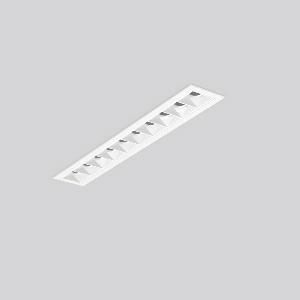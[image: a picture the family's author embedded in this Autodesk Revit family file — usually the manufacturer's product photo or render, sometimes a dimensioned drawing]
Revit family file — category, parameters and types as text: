
# Revit family: beamline_slim_641326_0025_2_76_4d5e
name_source: partatom
category: Lighting Fixtures
units: mm (PartAtom-declared; Revit-internal decimal feet)

## family parameters
Cut with Voids When Loaded = No
Host = Face
Light Source = No
Part Type = Normal
Room Calculation Point = No
Round Connector Dimension = Use Diameter
Shared = No

## types (1)
- BEAMLINE SLIM (1 x LED Modul 940, 2100 lm, 4000)
    Apparent Load = 25 VA
    CIE Flux Codes = 100 100 100 100 100
    Color Rendering = 92
    Color Temperature = 4000
    Default Elevation = 1800 mm
    Description = Series: BEAMLINE SLIM
Minimalistic recessed ceiling luminaire for aesthetically sophisticated lighting. Housing: metal, powder-coated. Perfect heat management with an aluminium heat sink. LED light unit with MRS technology: Mini-Reflector-System made of metallised thermoplastic with prismatic white glare-suppressing frame for pleasant glare-free light (RUG < 10). Narrow beam light distribution. Ceiling installation with spring system. Including separate LED converter with connecting cable 450 mm. 
Colour: traffic white, matt (RAL 9016)
Length: 295 mm
Width: 45 mm
Height: 1.5 mm
Cut-out length: 290 mm
Cut-out width: 40 mm
Recess height: 110 mm
Luminaire: recess height: 60 mm
Lamp: LED
Socket: without socket
Colour temperature: 4000K
Colour rendering index (CRI): 90
System power: 25 W
Rated luminous flux: 2100 lm
Luminous efficiency: 84 lm/W
Control gear: Converter, dimmable, DALI
Protection class: II
Type of protection: IP 20
    Height = 0 mm  [stored 0 ft]
    Lamp = 1 x LED Modul 940
    Lamp Light Flux = 2100 lm
    Lamp count = 1
    Length = 295 mm
    Lifetime = 50000 h
    Luminous efficacy = 84 lm/W
    Manufacturer = RZB
    ModVariant = No
    Model = 641326.0025.2.76
    Mounting Place = Ceiling
    Mounting Type = Recessed
    Number of Poles = 1
    OnlyDefault = Yes
    Power Factor = 1
    Product Name = BEAMLINE SLIM
    Product group = Recessed LED linear luminaires
    ProductGroupID = 407
    Protection Class = Protection class II
    Protection Degree = IP 20
    RLX_Detail_Level = 1
    RLX_Emergency_Light_Flux = 0 lm
    RLX_Emergency_Type = 0
    RLX_Emergency_Type_DB = No
    RlxData = <blob elided: 14005 chars, md5=0e648e52>
    Socket = socket
    Standby Power = 0 W
    System Light Flux = 2100 lm
    System Power = 25 W
    Type Comments = Product without accessories
    Type Image = 641326.0025.jpg
    URL = http://relux.com
    VarID = ---
    Voltage = 230 V
    Voltage Range = 220-240 V
    Weight = 0.00 kg
    Width = 45 mm

note: [stored X ft] marks values corroborated as IEEE doubles in the binary element streams (Revit-internal decimal feet)

## geometry (parser evidence)
native form markers: Sweep x11
no freeform markers — native parametric forms only
